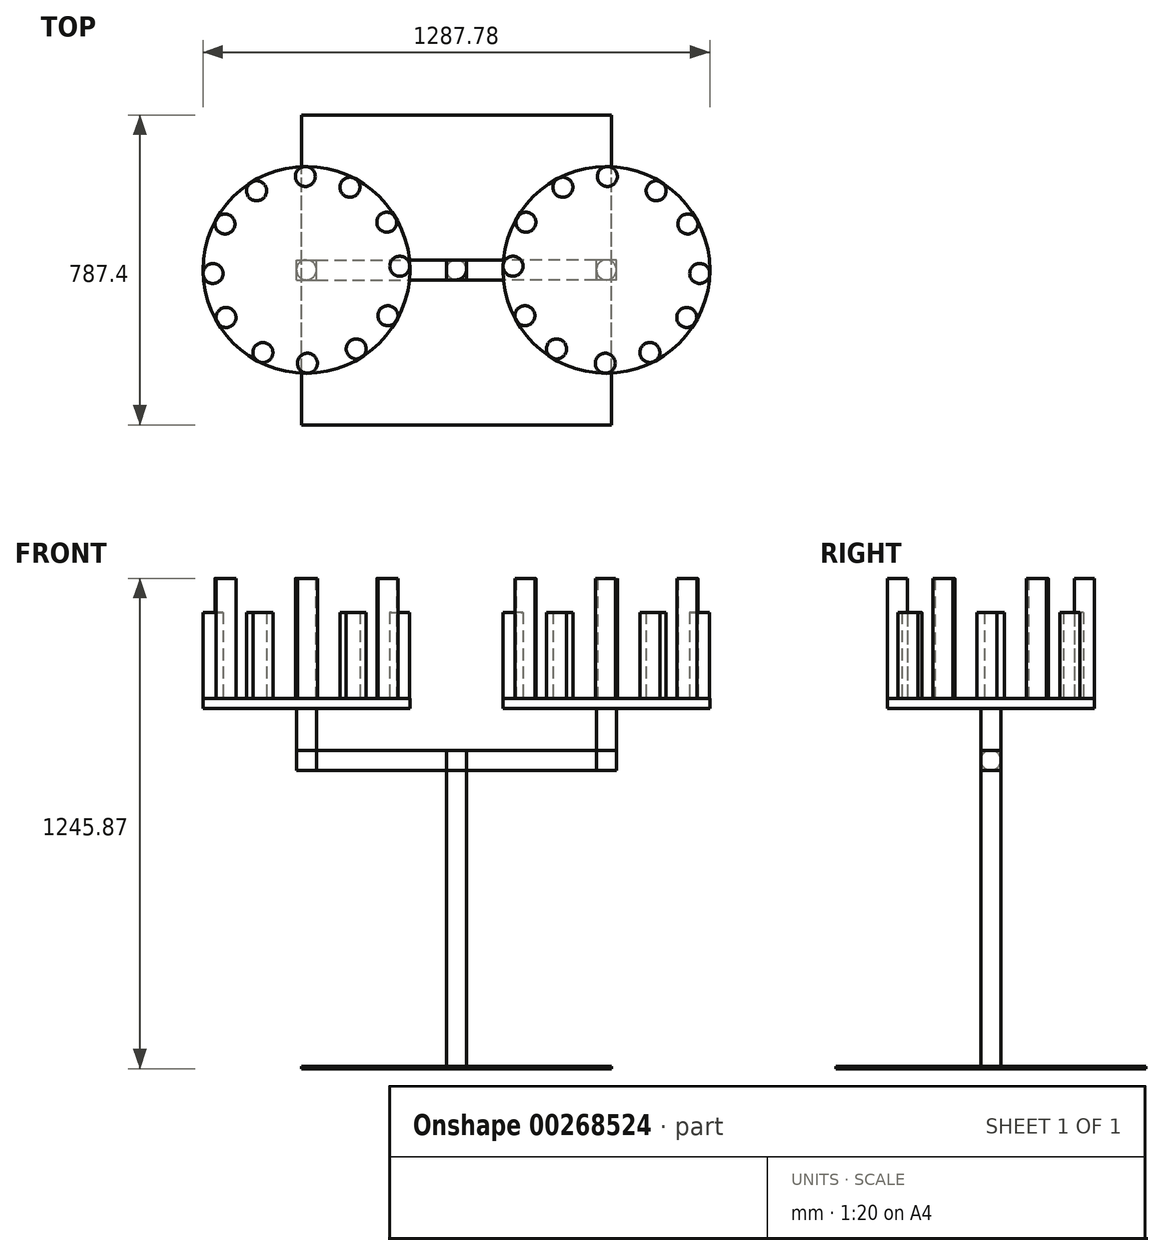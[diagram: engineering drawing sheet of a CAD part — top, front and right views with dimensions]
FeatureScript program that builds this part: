
annotation { "Feature Type Name" : "Feature", "Feature Type Description" : "" }
export const myFeature = defineFeature(function(context is Context, id is Id, definition is map)
    precondition{}
    {
        {
            var Q0;
            Q0=qCreatedBy(makeId("Top.planeOp"),FACE);
            var sketch = newSketch(context, id + "F0", { "sketchPlane" : qUnion([Q0])});
            skCircle(sketch, "E0", {"center": v(0, 0) * mm, "radius": 25.4 * mm});
            skSolve(sketch);
        }
        {
            var Q0;
            Q0 = qSketchRegion(id + "F0", true);
            extrude(context, id + "F1", {"entities" : qUnion([Q0]), "depth" : 751.84 * mm});
        }
        {
            var Q0;
            Q0=makeQuery(id+"F1.opExtrude","CAP_FACE",FACE,{"disambiguationData":[OSD([sQuery(id+"F0.wireOp",EDGE,"E0")])],"isStart":false});
            var sketch = newSketch(context, id + "F2", { "sketchPlane" : qUnion([Q0])});
            skLineSegment(sketch, "E1.bottom", {"start": v(0, 25.4) * mm, "end": v(-25.4, 25.4) * mm});
            skLineSegment(sketch, "E1.top", {"start": v(0, -25.4) * mm, "end": v(-25.4, -25.4) * mm});
            skLineSegment(sketch, "E1.right", {"start": v(-25.4, 25.4) * mm, "end": v(-25.4, -25.4) * mm});
            skPoint(sketch, "E1.middle", {"position": v(0, 0) * mm});
            skLineSegment(sketch, "E2", {"start": v(0, 25.4) * mm, "end": v(0, -25.4) * mm});
            skPoint(sketch, "E1.left.start.orphan", {"position": v(25.4, 25.4) * mm});
            skPoint(sketch, "E3.orphan", {"position": v(25.4, -25.4) * mm});
            skSolve(sketch);
        }
        {
            var Q0;
            Q0 = qSketchRegion(id + "F2", true);
            extrude(context, id + "F3", {"entities" : qUnion([Q0]), "operationType" : NewBodyOperationType.ADD, "depth" : 50.8 * mm});
        }
        {
            var Q0;
            Q0=makeQuery(id+"F3.opExtrude","SWEPT_FACE",FACE,{"disambiguationData":[OSD([sQuery(id+"F2.wireOp",EDGE,"E1.right")])]});
            var sketch = newSketch(context, id + "F4", { "sketchPlane" : qUnion([Q0])});
            skCircle(sketch, "E4", {"center": v(0, 777.24) * mm, "radius": 25.4 * mm});
            skPoint(sketch, "E4.centerSnap0", {"position": v(25.4, 777.24) * mm});
            skSolve(sketch);
        }
        {
            var Q0;
            Q0 = qSketchRegion(id + "F4", true);
            extrude(context, id + "F5", {"entities" : qUnion([Q0]), "operationType" : NewBodyOperationType.ADD, "depth" : 330.2 * mm});
        }
        {
            var Q0;
            Q0=makeQuery(id+"F5.opExtrude","CAP_FACE",FACE,{"disambiguationData":[OSD([sQuery(id+"F4.wireOp",EDGE,"E4")])],"isStart":false});
            var sketch = newSketch(context, id + "F6", { "sketchPlane" : qUnion([Q0])});
            skLineSegment(sketch, "E5.bottom", {"start": v(25.4, 802.64) * mm, "end": v(-25.4, 802.64) * mm});
            skLineSegment(sketch, "E5.top", {"start": v(25.4, 751.84) * mm, "end": v(-25.4, 751.84) * mm});
            skLineSegment(sketch, "E5.left", {"start": v(25.4, 802.64) * mm, "end": v(25.4, 751.84) * mm});
            skLineSegment(sketch, "E5.right", {"start": v(-25.4, 802.64) * mm, "end": v(-25.4, 751.84) * mm});
            skPoint(sketch, "E5.middle", {"position": v(0, 777.24) * mm});
            skSolve(sketch);
        }
        {
            var Q0;
            Q0 = qSketchRegion(id + "F6", true);
            extrude(context, id + "F7", {"entities" : qUnion([Q0]), "operationType" : NewBodyOperationType.ADD, "depth" : 50.8 * mm});
        }
        {
            var Q0;
            Q0=makeQuery(id+"F7.opExtrude","SWEPT_FACE",FACE,{"disambiguationData":[OSD([sQuery(id+"F6.wireOp",EDGE,"E5.bottom")])]});
            var sketch = newSketch(context, id + "F8", { "sketchPlane" : qUnion([Q0])});
            skCircle(sketch, "E6", {"center": v(-381, 0) * mm, "radius": 25.4 * mm});
            skPoint(sketch, "E6.centerSnap0", {"position": v(-381, -25.4) * mm});
            skSolve(sketch);
        }
        {
            var Q0;
            Q0 = qSketchRegion(id + "F8", true);
            extrude(context, id + "F9", {"entities" : qUnion([Q0]), "operationType" : NewBodyOperationType.ADD, "depth" : 106.68 * mm});
        }
        {
            var Q0;
            Q0=makeQuery(id+"F9.opExtrude","CAP_FACE",FACE,{"disambiguationData":[OSD([sQuery(id+"F8.wireOp",EDGE,"E6")])],"isStart":false});
            var sketch = newSketch(context, id + "F10", { "sketchPlane" : qUnion([Q0])});
            skCircle(sketch, "E7", {"center": v(-381, 0) * mm, "radius": 262.9 * mm});
            skSolve(sketch);
        }
        {
            var Q0;
            Q0 = qSketchRegion(id + "F10", true);
            extrude(context, id + "F11", {"entities" : qUnion([Q0]), "operationType" : NewBodyOperationType.ADD, "depth" : 25.4 * mm});
        }
        {
            var Q0;
            Q0=makeQuery(id+"F11.opExtrude","CAP_FACE",FACE,{"disambiguationData":[OSD([sQuery(id+"F10.wireOp",EDGE,"E7")])],"isStart":false});
            var sketch = newSketch(context, id + "F12", { "sketchPlane" : qUnion([Q0])});
            skCircle(sketch, "E8", {"center": v(-383.69, 237.37) * mm, "radius": 25.4 * mm});
            skSolve(sketch);
        }
        {
            var Q0;
            Q0 = qSketchRegion(id + "F12", true);
            extrude(context, id + "F13", {"entities" : qUnion([Q0]), "depth" : 304.8 * mm});
        }
        {
            var Q0;
            Q0=makeQuery(id+"F13.opExtrude","SWEPT_BODY",BODY,{"disambiguationData":[OSD([sQuery(id+"F12.wireOp",EDGE,"E8")])]});
            var Q1;
            Q1=makeQuery(id+"F11.opExtrude","CAP_EDGE",EDGE,{"disambiguationData":[OSD([sQuery(id+"F10.wireOp",EDGE,"E7")])],"isStart":false});
            circularPattern(context, id + "F14", {"entities" : qUnion([Q0]), "axis" : qUnion([Q1]), "angle" : 360 * degree, "instanceCount" : 6, "equalSpace" : true});
        }
        {
            var Q0;
            Q0=makeQuery(id+"F11.opExtrude","CAP_FACE",FACE,{"disambiguationData":[OSD([sQuery(id+"F10.wireOp",EDGE,"E7")])],"isStart":false});
            var sketch = newSketch(context, id + "F15", { "sketchPlane" : qUnion([Q0])});
            skCircle(sketch, "E9", {"center": v(-507.58, 200.79) * mm, "radius": 25.4 * mm});
            skSolve(sketch);
        }
        {
            var Q0;
            Q0 = qSketchRegion(id + "F15", true);
            extrude(context, id + "F16", {"entities" : qUnion([Q0]), "depth" : 218.44 * mm});
        }
        {
            var Q0;
            Q0=makeQuery(id+"F16.opExtrude","SWEPT_BODY",BODY,{"disambiguationData":[OSD([sQuery(id+"F15.wireOp",EDGE,"E9")])]});
            var Q1;
            Q1=makeQuery(id+"F11.opExtrude","CAP_EDGE",EDGE,{"disambiguationData":[OSD([sQuery(id+"F10.wireOp",EDGE,"E7")])],"isStart":false});
            circularPattern(context, id + "F17", {"entities" : qUnion([Q0]), "axis" : qUnion([Q1]), "angle" : 360 * degree, "instanceCount" : 6, "equalSpace" : true});
        }
        {
            var Q0;
            Q0=makeQuery(id+"F14.opPattern","COPY",BODY,{"derivedFrom":makeQuery(id+"F13.opExtrude","SWEPT_BODY",BODY,{"disambiguationData":[OSD([sQuery(id+"F12.wireOp",EDGE,"E8")])]}),"instanceName":"3"});
            var Q1;
            Q1=makeQuery(id+"F17.opPattern","COPY",BODY,{"derivedFrom":makeQuery(id+"F16.opExtrude","SWEPT_BODY",BODY,{"disambiguationData":[OSD([sQuery(id+"F15.wireOp",EDGE,"E9")])]}),"instanceName":"2"});
            var Q2;
            Q2=makeQuery(id+"F17.opPattern","COPY",BODY,{"derivedFrom":makeQuery(id+"F16.opExtrude","SWEPT_BODY",BODY,{"disambiguationData":[OSD([sQuery(id+"F15.wireOp",EDGE,"E9")])]}),"instanceName":"1"});
            var Q3;
            Q3=makeQuery(id+"F17.opPattern","COPY",BODY,{"derivedFrom":makeQuery(id+"F16.opExtrude","SWEPT_BODY",BODY,{"disambiguationData":[OSD([sQuery(id+"F15.wireOp",EDGE,"E9")])]}),"instanceName":"4"});
            var Q4;
            Q4=makeQuery(id+"F16.opExtrude","SWEPT_BODY",BODY,{"disambiguationData":[OSD([sQuery(id+"F15.wireOp",EDGE,"E9")])]});
            var Q5;
            Q5=makeQuery(id+"F14.opPattern","COPY",BODY,{"derivedFrom":makeQuery(id+"F13.opExtrude","SWEPT_BODY",BODY,{"disambiguationData":[OSD([sQuery(id+"F12.wireOp",EDGE,"E8")])]}),"instanceName":"5"});
            var Q6;
            Q6=makeQuery(id+"F14.opPattern","COPY",BODY,{"derivedFrom":makeQuery(id+"F13.opExtrude","SWEPT_BODY",BODY,{"disambiguationData":[OSD([sQuery(id+"F12.wireOp",EDGE,"E8")])]}),"instanceName":"2"});
            var Q7;
            Q7=makeQuery(id+"F1.opExtrude","SWEPT_BODY",BODY,{"disambiguationData":[OSD([sQuery(id+"F0.wireOp",EDGE,"E0")])]});
            var Q8;
            Q8=makeQuery(id+"F13.opExtrude","SWEPT_BODY",BODY,{"disambiguationData":[OSD([sQuery(id+"F12.wireOp",EDGE,"E8")])]});
            var Q9;
            Q9=makeQuery(id+"F17.opPattern","COPY",BODY,{"derivedFrom":makeQuery(id+"F16.opExtrude","SWEPT_BODY",BODY,{"disambiguationData":[OSD([sQuery(id+"F15.wireOp",EDGE,"E9")])]}),"instanceName":"5"});
            var Q10;
            Q10=makeQuery(id+"F14.opPattern","COPY",BODY,{"derivedFrom":makeQuery(id+"F13.opExtrude","SWEPT_BODY",BODY,{"disambiguationData":[OSD([sQuery(id+"F12.wireOp",EDGE,"E8")])]}),"instanceName":"1"});
            var Q11;
            Q11=makeQuery(id+"F17.opPattern","COPY",BODY,{"derivedFrom":makeQuery(id+"F16.opExtrude","SWEPT_BODY",BODY,{"disambiguationData":[OSD([sQuery(id+"F15.wireOp",EDGE,"E9")])]}),"instanceName":"3"});
            var Q12;
            Q12=makeQuery(id+"F14.opPattern","COPY",BODY,{"derivedFrom":makeQuery(id+"F13.opExtrude","SWEPT_BODY",BODY,{"disambiguationData":[OSD([sQuery(id+"F12.wireOp",EDGE,"E8")])]}),"instanceName":"4"});
            var Q13;
            Q13=makeQuery(id+"F3.opExtrude","SWEPT_FACE",FACE,{"disambiguationData":[OSD([sQuery(id+"F2.wireOp",EDGE,"E2")])]});
            mirror(context, id + "F18", {"operationType" : NewBodyOperationType.ADD, "entities" : qUnion([Q0, Q1, Q2, Q3, Q4, Q5, Q6, Q7, Q8, Q9, Q10, Q11, Q12]), "mirrorPlane" : qUnion([Q13])});
        }
        {
            var Q0;
            Q0=makeQuery(id+"F1.opExtrude","CAP_FACE",FACE,{"disambiguationData":[OSD([sQuery(id+"F0.wireOp",EDGE,"E0")])],"isStart":true});
            var sketch = newSketch(context, id + "F19", { "sketchPlane" : qUnion([Q0])});
            skLineSegment(sketch, "E10.bottom", {"start": v(393.7, 393.7) * mm, "end": v(-393.7, 393.7) * mm});
            skLineSegment(sketch, "E10.top", {"start": v(393.7, -393.7) * mm, "end": v(-393.7, -393.7) * mm});
            skLineSegment(sketch, "E10.left", {"start": v(393.7, 393.7) * mm, "end": v(393.7, -393.7) * mm});
            skLineSegment(sketch, "E10.right", {"start": v(-393.7, 393.7) * mm, "end": v(-393.7, -393.7) * mm});
            skPoint(sketch, "E10.middle", {"position": v(0, 0) * mm});
            skSolve(sketch);
        }
        {
            var Q0;
            Q0 = qSketchRegion(id + "F19", true);
            extrude(context, id + "F20", {"entities" : qUnion([Q0]), "operationType" : NewBodyOperationType.ADD, "depth" : 6.35 * mm});
        }
    });
